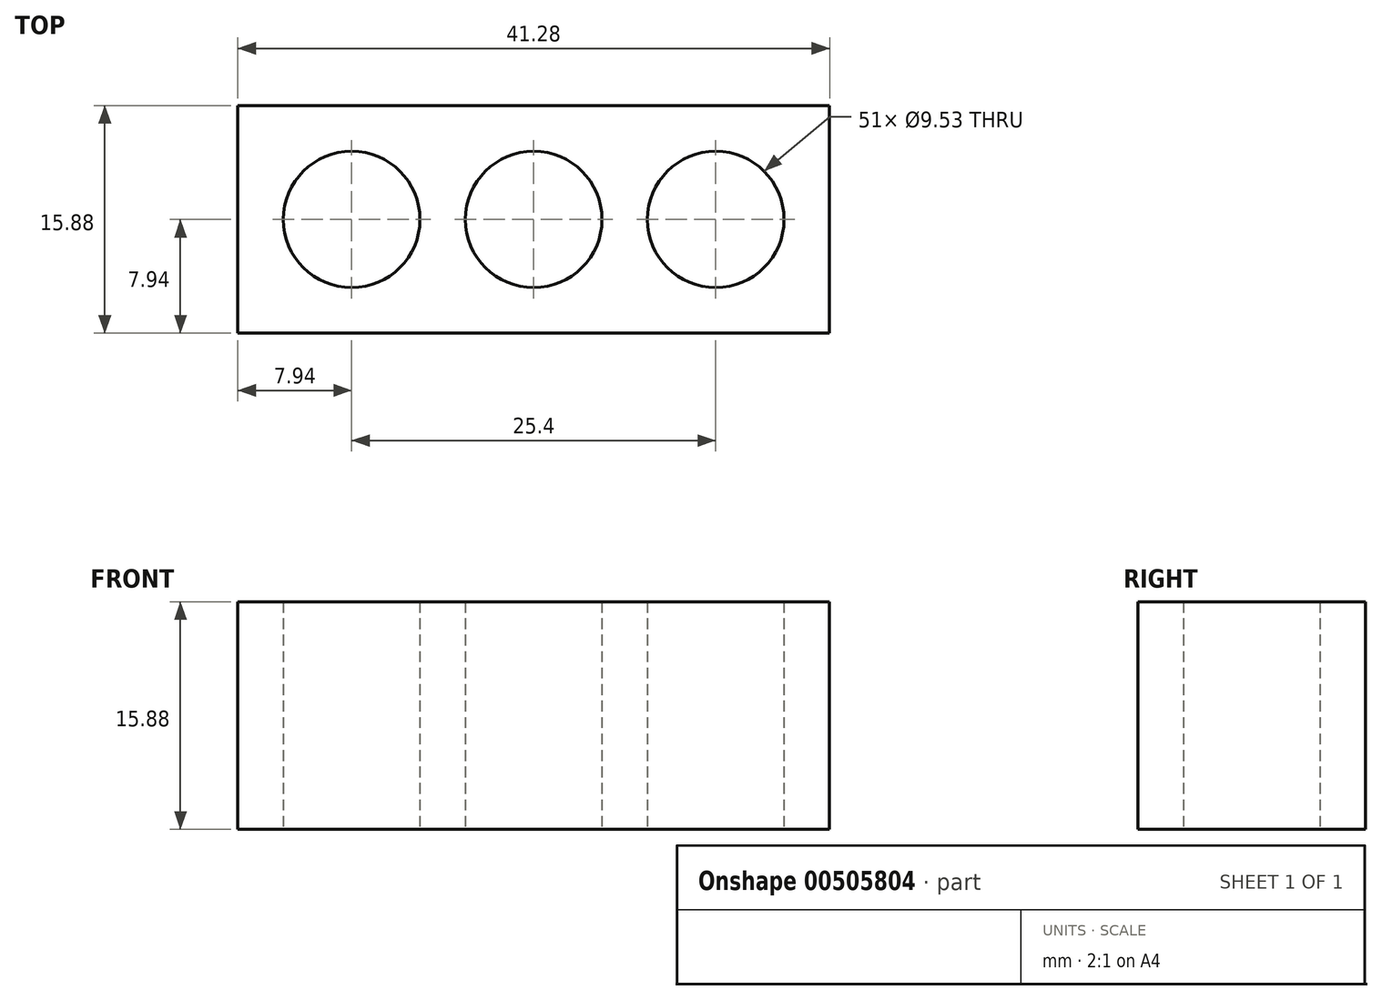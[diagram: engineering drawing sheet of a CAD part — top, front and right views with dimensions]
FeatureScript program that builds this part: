
annotation { "Feature Type Name" : "Feature", "Feature Type Description" : "" }
export const myFeature = defineFeature(function(context is Context, id is Id, definition is map)
    precondition{}
    {
        {
            var Q0;
            Q0=qCreatedBy(makeId("Front.planeOp"),FACE);
            var sketch = newSketch(context, id + "F0", { "sketchPlane" : qUnion([Q0])});
            skLineSegment(sketch, "E0.bottom", {"start": v(20.64, 7.94) * mm, "end": v(-20.64, 7.94) * mm});
            skLineSegment(sketch, "E0.top", {"start": v(20.64, -7.94) * mm, "end": v(-20.64, -7.94) * mm});
            skLineSegment(sketch, "E0.left", {"start": v(20.64, 7.94) * mm, "end": v(20.64, -7.94) * mm});
            skLineSegment(sketch, "E0.right", {"start": v(-20.64, 7.94) * mm, "end": v(-20.64, -7.94) * mm});
            skPoint(sketch, "E0.middle", {"position": v(0, 0) * mm});
            skCircle(sketch, "E1", {"center": v(0, 0) * mm, "radius": 4.76 * mm});
            skLineSegment(sketch, "E2", {"start": v(0, 0) * mm, "end": v(12.7, 0) * mm, "construction": true});
            skCircle(sketch, "E3", {"center": v(12.7, 0) * mm, "radius": 4.76 * mm});
            skCircle(sketch, "E4.MirrorC", {"center": v(-12.7, 0) * mm, "radius": 4.76 * mm});
            skSolve(sketch);
        }
        {
            var Q0;
            Q0=qSketchRegion(id+"F0",true);
            extrude(context, id + "F1", {"entities" : qUnion([Q0]), "oppositeDirection" : true, "depth" : 15.88 * mm});
        }
        {
            var Q0;
            Q0=makeQuery(id+"F1.opExtrude","SWEPT_BODY",BODY,{"disambiguationData":[OSD([sQuery(id+"F0.wireOp",EDGE,"E0.bottom"),sQuery(id+"F0.wireOp",EDGE,"E0.top"),sQuery(id+"F0.wireOp",EDGE,"E0.left"),sQuery(id+"F0.wireOp",EDGE,"E0.right"),sQuery(id+"F0.wireOp",EDGE,"E1"),sQuery(id+"F0.wireOp",EDGE,"E3"),sQuery(id+"F0.wireOp",EDGE,"E4.MirrorC")])]});
            var Q1;
            Q1=sQuery(id+"F0.wireOp",EDGE,"E2");
            transform(context, id + "F2", {"entities" : qUnion([Q0]), "transformType" : TransformType.ROTATION, "transformAxis" : qUnion([Q1]), "angle" : 90 * degree, "makeCopy" : false});
        }
    });
